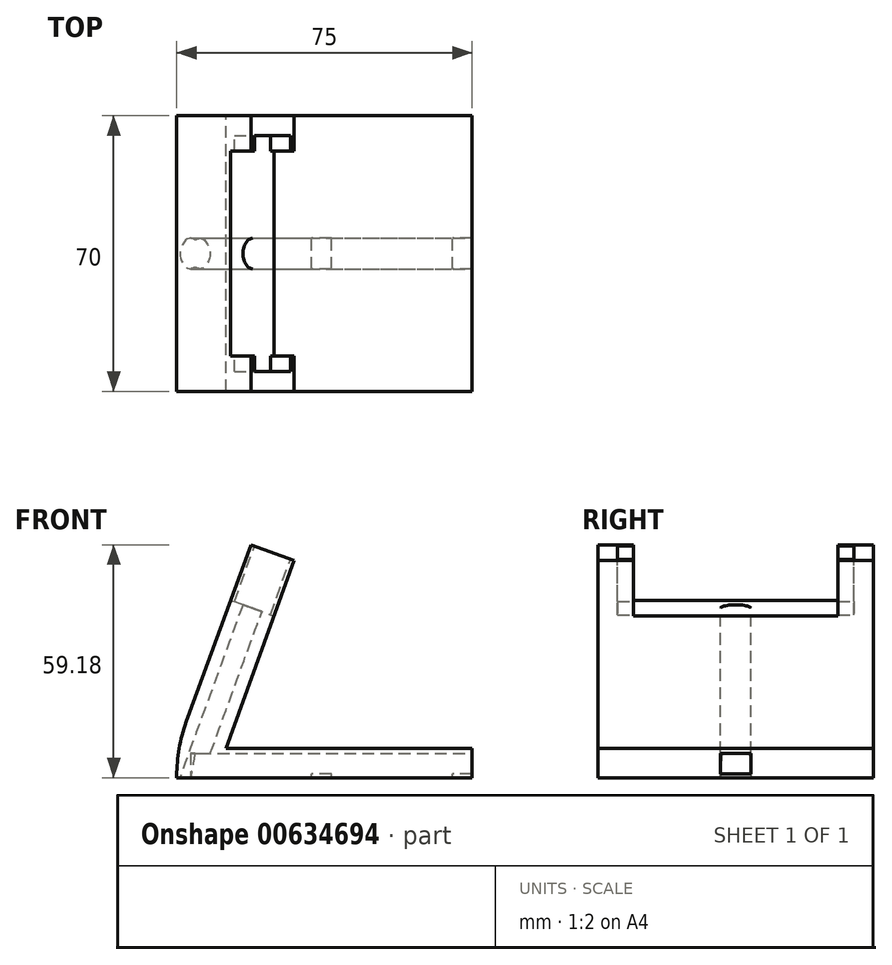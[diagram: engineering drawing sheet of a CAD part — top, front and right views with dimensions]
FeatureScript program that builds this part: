
annotation { "Feature Type Name" : "Feature", "Feature Type Description" : "" }
export const myFeature = defineFeature(function(context is Context, id is Id, definition is map)
    precondition{}
    {
        {
            var Q0;
            Q0=qCreatedBy(makeId("Front.planeOp"),FACE);
            var sketch = newSketch(context, id + "F0", { "sketchPlane" : qUnion([Q0])});
            skLineSegment(sketch, "E0.bottom", {"start": v(0, 0) * mm, "end": v(-75, 0) * mm});
            skLineSegment(sketch, "E0.top", {"start": v(0, 7.5) * mm, "end": v(-75, 7.5) * mm});
            skLineSegment(sketch, "E0.left", {"start": v(0, 0) * mm, "end": v(0, 7.5) * mm});
            skLineSegment(sketch, "E0.right", {"start": v(-75, 0) * mm, "end": v(-75, 7.5) * mm});
            skLineSegment(sketch, "E1", {"start": v(-75, 7.5) * mm, "end": v(-56.19, 59.18) * mm});
            skLineSegment(sketch, "E2", {"start": v(-45.15, 55.16) * mm, "end": v(-62.5, 7.5) * mm});
            skLineSegment(sketch, "E3", {"start": v(-56.19, 59.18) * mm, "end": v(-45.15, 55.16) * mm});
            skLineSegment(sketch, "E4", {"start": v(-62.5, 7.5) * mm, "end": v(-73.54, 11.52) * mm, "construction": true});
            skLineSegment(sketch, "E5", {"start": v(-68.02, 9.5) * mm, "end": v(-78.28, -18.68) * mm, "construction": true});
            skSolve(sketch);
        }
        {
            var Q0;
            {var subQ0=sQuery(id+"F0.wireOp",EDGE,"E1");Q0=makeQuery(id+"F0.imprint","IMPRINT",FACE,{"disambiguationData":[TD([[makeQuery(id+"F0.imprint","IMPRINT",EDGE,{"derivedFrom":subQ0}),-1.0]])]});}
            var Q1;
            Q1=makeQuery(id+"F0.imprint","IMPRINT",FACE,{"disambiguationData":[TD([[makeQuery(id+"F0.imprint","IMPRINT",EDGE,{"derivedFrom":sQuery(id+"F0.wireOp",EDGE,"E0.bottom")}),-1.0]])]});
            extrude(context, id + "F1", {"entities" : qUnion([Q0, Q1]), "depth" : 70 * mm, "offsetDistance" : 25 * mm});
        }
        {
            var Q0;
            Q0=makeQuery(id+"F1.opExtrude","SWEPT_FACE",FACE,{"disambiguationData":[OSD([sQuery(id+"F0.wireOp",EDGE,"E3")])]});
            var sketch = newSketch(context, id + "F2", { "sketchPlane" : qUnion([Q0])});
            skLineSegment(sketch, "E6.bottom", {"start": v(-61.3, 0) * mm, "end": v(-73.04, 0) * mm});
            skLineSegment(sketch, "E6.top", {"start": v(-61.3, -70) * mm, "end": v(-73.04, -70) * mm});
            skLineSegment(sketch, "E6.left", {"start": v(-61.3, 0) * mm, "end": v(-61.3, -70) * mm});
            skLineSegment(sketch, "E6.right", {"start": v(-73.04, 0) * mm, "end": v(-73.04, -70) * mm});
            skLineSegment(sketch, "E7", {"start": v(-73.04, -65) * mm, "end": v(-61.3, -65) * mm});
            skLineSegment(sketch, "E8", {"start": v(-73.04, -5) * mm, "end": v(-61.3, -5) * mm});
            skLineSegment(sketch, "E9", {"start": v(-72.04, -70) * mm, "end": v(-72.04, 0) * mm});
            skLineSegment(sketch, "E10", {"start": v(-62.3, -70) * mm, "end": v(-62.3, 0) * mm});
            skLineSegment(sketch, "E11", {"start": v(-73.04, -61) * mm, "end": v(-72.04, -61) * mm});
            skLineSegment(sketch, "E12", {"start": v(-73.04, -9) * mm, "end": v(-72.04, -9) * mm});
            skLineSegment(sketch, "E13", {"start": v(-62.3, -61) * mm, "end": v(-61.3, -61) * mm});
            skLineSegment(sketch, "E14", {"start": v(-62.3, -9) * mm, "end": v(-61.3, -9) * mm});
            skLineSegment(sketch, "E15", {"start": v(-67.17, -65) * mm, "end": v(-67.17, -5) * mm, "construction": true});
            skLineSegment(sketch, "E16", {"start": v(-72.04, -35) * mm, "end": v(-62.3, -35) * mm, "construction": true});
            skLineSegment(sketch, "E17", {"start": v(-67.17, -35) * mm, "end": v(-67.17, -31.65) * mm, "construction": true});
            skLineSegment(sketch, "E18", {"start": v(-67.17, -35) * mm, "end": v(-67.17, -38.35) * mm, "construction": true});
            skLineSegment(sketch, "E19", {"start": v(-67.17, -38.35) * mm, "end": v(-67.92, -38.35) * mm, "construction": true});
            skLineSegment(sketch, "E20", {"start": v(-67.17, -31.65) * mm, "end": v(-66.42, -31.65) * mm, "construction": true});
            skLineSegment(sketch, "E21", {"start": v(-67.17, -31.65) * mm, "end": v(-67.92, -31.65) * mm, "construction": true});
            skLineSegment(sketch, "E22", {"start": v(-67.17, -38.35) * mm, "end": v(-66.42, -38.35) * mm, "construction": true});
            skLineSegment(sketch, "E23", {"start": v(-66.42, -38.35) * mm, "end": v(-66.42, -31.65) * mm, "construction": true});
            skLineSegment(sketch, "E24", {"start": v(-67.92, -38.35) * mm, "end": v(-67.92, -31.65) * mm, "construction": true});
            skLineSegment(sketch, "E25", {"start": v(-67.17, -35) * mm, "end": v(-69.74, -35) * mm, "construction": true});
            skLineSegment(sketch, "E26", {"start": v(-67.17, -35) * mm, "end": v(-64.6, -35) * mm, "construction": true});
            skLineSegment(sketch, "E27", {"start": v(-67.17, -35) * mm, "end": v(-67.17, -38.88) * mm, "construction": true});
            skLineSegment(sketch, "E28", {"start": v(-67.17, -35) * mm, "end": v(-67.17, -31.13) * mm, "construction": true});
            skFitSpline(sketch, "E29", {"points": [v(-67.17, -38.88) * mm, v(-69.74, -35) * mm, v(-67.17, -31.13) * mm, v(-64.6, -35) * mm, v(-67.17, -38.88) * mm]});
            skSolve(sketch);
        }
        {
            var Q0;
            {var subQ0=sQuery(id+"F2.wireOp",EDGE,"E11");Q0=makeQuery(id+"F2.imprint","IMPRINT",FACE,{"disambiguationData":[TD([[makeQuery(id+"F2.imprint","IMPRINT",EDGE,{"derivedFrom":subQ0}),1.0]])]});}
            var Q1;
            {var subQ0=sQuery(id+"F2.wireOp",EDGE,"E13");Q1=makeQuery(id+"F2.imprint","IMPRINT",FACE,{"disambiguationData":[TD([[makeQuery(id+"F2.imprint","IMPRINT",EDGE,{"derivedFrom":subQ0}),1.0]])]});}
            var Q2;
            Q2=makeQuery(id+"F2.imprint","IMPRINT",FACE,{"disambiguationData":[TD([[makeQuery(id+"F2.imprint","IMPRINT",EDGE,{"derivedFrom":sQuery(id+"F2.wireOp",EDGE,"E29")}),1.0]])]});
            extrude(context, id + "F3", {"entities" : qUnion([Q0, Q1, Q2]), "operationType" : NewBodyOperationType.REMOVE, "oppositeDirection" : true, "depth" : 15 * mm, "offsetDistance" : 25 * mm});
        }
        {
            var Q0;
            Q0=makeQuery(id+"F3.boolean.opBoolean","SPLIT",FACE,{"disambiguationData":[TD([makeQuery(id+"F3.opExtrude","SWEPT_FACE",FACE,{"disambiguationData":[OSD([sQuery(id+"F2.wireOp",EDGE,"E29")])]})])],"derivedFrom":makeQuery(id+"F1.opExtrude","SWEPT_FACE",FACE,{"disambiguationData":[OSD([sQuery(id+"F0.wireOp",EDGE,"E3")])]})});
            extrude(context, id + "F4", {"entities" : qUnion([Q0]), "operationType" : NewBodyOperationType.REMOVE, "oppositeDirection" : true, "depth" : 65 * mm, "offsetDistance" : 25 * mm});
        }
        {
            var Q0;
            Q0=makeQuery(id+"F1.opExtrude","SWEPT_FACE",FACE,{"disambiguationData":[OSD([sQuery(id+"F0.wireOp",EDGE,"E0.bottom")])]});
            var sketch = newSketch(context, id + "F5", { "sketchPlane" : qUnion([Q0])});
            skLineSegment(sketch, "E30", {"start": v(-75, 35) * mm, "end": v(0, 35) * mm, "construction": true});
            skLineSegment(sketch, "E31", {"start": v(-74.22, 35) * mm, "end": v(-68.74, 35) * mm, "construction": true});
            skLineSegment(sketch, "E32", {"start": v(-71.48, 35) * mm, "end": v(-71.48, 38.87) * mm});
            skLineSegment(sketch, "E33", {"start": v(-71.48, 35) * mm, "end": v(-71.48, 31.12) * mm});
            skLineSegment(sketch, "E34", {"start": v(-71.48, 31.12) * mm, "end": v(0, 31.12) * mm});
            skLineSegment(sketch, "E35", {"start": v(-71.48, 38.87) * mm, "end": v(0, 38.87) * mm});
            skLineSegment(sketch, "E36", {"start": v(0, 31.12) * mm, "end": v(0, 38.87) * mm});
            skSolve(sketch);
        }
        {
            var Q0;
            {var subQ0=sQuery(id+"F5.wireOp",EDGE,"E34");Q0=makeQuery(id+"F5.imprint","IMPRINT",FACE,{"disambiguationData":[TD([[makeQuery(id+"F5.imprint","IMPRINT",EDGE,{"derivedFrom":subQ0}),1.0]])]});}
            extrude(context, id + "F6", {"entities" : qUnion([Q0]), "operationType" : NewBodyOperationType.REMOVE, "oppositeDirection" : true, "depth" : 6.2 * mm, "offsetDistance" : 25 * mm});
        }
        {
            var Q0;
            Q0=makeQuery(id+"F6.boolean.opBoolean","COPY",FACE,{"derivedFrom":makeQuery(id+"F6.opExtrude","SWEPT_FACE",FACE,{"disambiguationData":[OSD([sQuery(id+"F5.wireOp",EDGE,"E34")])]})});
            var sketch = newSketch(context, id + "F7", { "sketchPlane" : qUnion([Q0])});
            skLineSegment(sketch, "E37.bottom", {"start": v(0, 0) * mm, "end": v(-5, 0) * mm});
            skLineSegment(sketch, "E37.top", {"start": v(0, 1) * mm, "end": v(-5, 1) * mm});
            skLineSegment(sketch, "E37.left", {"start": v(0, 0) * mm, "end": v(0, 1) * mm});
            skLineSegment(sketch, "E37.right", {"start": v(-5, 0) * mm, "end": v(-5, 1) * mm});
            skLineSegment(sketch, "E38.bottom", {"start": v(-35.74, 0) * mm, "end": v(-40.74, 0) * mm});
            skLineSegment(sketch, "E38.top", {"start": v(-35.74, 1) * mm, "end": v(-40.74, 1) * mm});
            skLineSegment(sketch, "E38.left", {"start": v(-35.74, 0) * mm, "end": v(-35.74, 1) * mm});
            skLineSegment(sketch, "E38.right", {"start": v(-40.74, 0) * mm, "end": v(-40.74, 1) * mm});
            skSolve(sketch);
        }
        {
            var Q0;
            Q0=makeQuery(id+"F7.imprint","IMPRINT",FACE,{"disambiguationData":[TD([[makeQuery(id+"F7.imprint","IMPRINT",EDGE,{"derivedFrom":sQuery(id+"F7.wireOp",EDGE,"E38.bottom")}),1.0]])]});
            var Q1;
            Q1=makeQuery(id+"F7.imprint","IMPRINT",FACE,{"disambiguationData":[TD([[makeQuery(id+"F7.imprint","IMPRINT",EDGE,{"derivedFrom":sQuery(id+"F7.wireOp",EDGE,"E37.bottom")}),1.0]])]});
            extrude(context, id + "F8", {"entities" : qUnion([Q0, Q1]), "operationType" : NewBodyOperationType.ADD, "depth" : 7.75 * mm, "offsetDistance" : 25 * mm});
        }
        {
            var Q0;
            Q0=makeQuery(id+"F1.opExtrude","SWEPT_EDGE",EDGE,{"disambiguationData":[OSD([sQuery(id+"F0.wireOp",EDGE,"E0.top"),sQuery(id+"F0.wireOp",EDGE,"E0.right"),sQuery(id+"F0.wireOp",EDGE,"E1")])]});
            fillet(context, id + "F9", {"entities" : qUnion([Q0]), "radius" : 40 * mm, "tangentPropagation" : true, "allowEdgeOverflow" : false});
        }
    });
